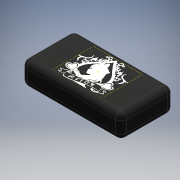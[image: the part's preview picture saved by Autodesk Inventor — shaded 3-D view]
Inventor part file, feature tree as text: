
AUTODESK INVENTOR PART (.ipt)
format: ipt  version: 2016 (Build 200138000, 138)  size: 279,040 bytes
history: native  units: mm
features: other x3, sketch x3, extrude x1, fillet x1
ambient origin geometry x8: Origin, YZ Plane, XZ Plane, XY Plane, X Axis, Y Axis, Z Axis, Center Point
bodies: Body1 (feature_tree)
feature tree (8):
  other  "ソリッド2"
  extrude  "押し出し1"  Depth=34.0mm
  fillet  "フィレット1"  Radius=18.0mm
  sketch  "スケッチ3"
  sketch  "スケッチ4"
  sketch  "スケッチ2"
  other  "イメージ1"
  other  "イメージ2"
